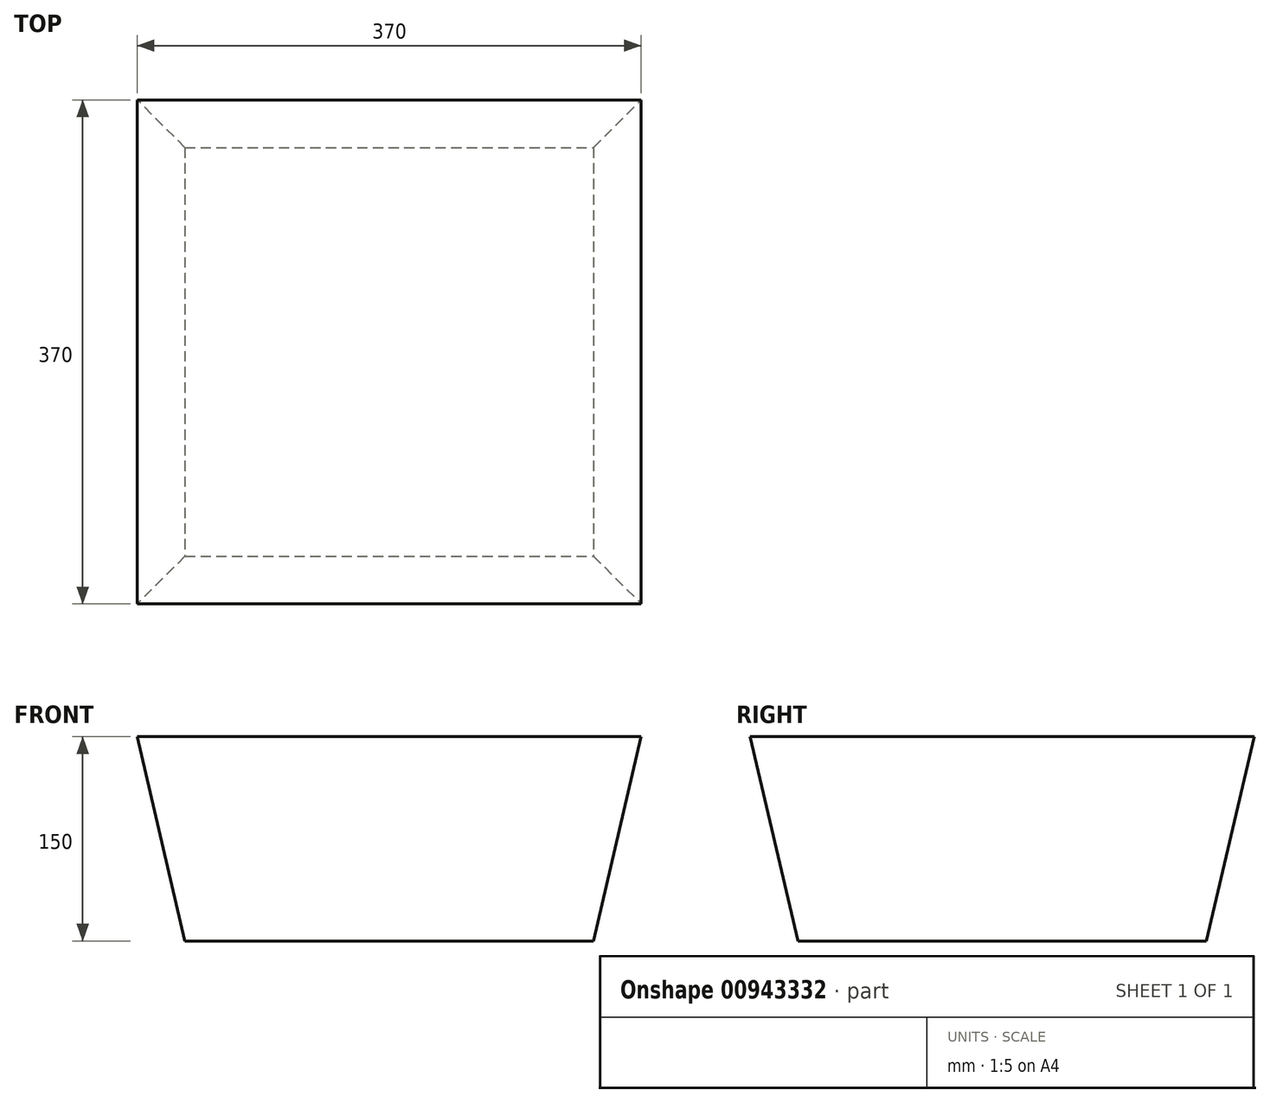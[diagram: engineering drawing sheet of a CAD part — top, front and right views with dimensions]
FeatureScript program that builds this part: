
annotation { "Feature Type Name" : "Feature", "Feature Type Description" : "" }
export const myFeature = defineFeature(function(context is Context, id is Id, definition is map)
    precondition{}
    {
        {
            var Q0;
            Q0=qCreatedBy(makeId("Top.planeOp"),FACE);
            var sketch = newSketch(context, id + "F0", { "sketchPlane" : qUnion([Q0])});
            skLineSegment(sketch, "E0.bottom", {"start": v(0, 0) * mm, "end": v(370, 0) * mm});
            skLineSegment(sketch, "E0.top", {"start": v(0, 370) * mm, "end": v(370, 370) * mm});
            skLineSegment(sketch, "E0.left", {"start": v(0, 0) * mm, "end": v(0, 370) * mm});
            skLineSegment(sketch, "E0.right", {"start": v(370, 0) * mm, "end": v(370, 370) * mm});
            skSolve(sketch);
        }
        {
            var Q0;
            Q0=qCreatedBy(makeId("Top.planeOp"),FACE);
            cPlane(context, id + "F1", {"entities" : qUnion([Q0]), "cplaneType" : CPlaneType.OFFSET, "offset" : 150 * mm, "oppositeDirection" : true, "width" : 150 * mm, "height" : 150 * mm});
        }
        {
            var Q0;
            Q0=qCreatedBy(id+"F1.planeOp",FACE);
            var sketch = newSketch(context, id + "F2", { "sketchPlane" : qUnion([Q0])});
            skLineSegment(sketch, "E1.bottom", {"start": v(35, 335) * mm, "end": v(335, 335) * mm});
            skLineSegment(sketch, "E1.top", {"start": v(35, 35) * mm, "end": v(335, 35) * mm});
            skLineSegment(sketch, "E1.left", {"start": v(35, 335) * mm, "end": v(35, 35) * mm});
            skLineSegment(sketch, "E1.right", {"start": v(335, 335) * mm, "end": v(335, 35) * mm});
            skSolve(sketch);
        }
        {
            var Q0;
            Q0=makeQuery(id+"F2.imprint","IMPRINT",FACE,{"disambiguationData":[TD([[makeQuery(id+"F2.imprint","IMPRINT",EDGE,{"derivedFrom":sQuery(id+"F2.wireOp",EDGE,"E1.bottom")}),-1.0]])]});
            var Q1;
            Q1=makeQuery(id+"F0.imprint","IMPRINT",FACE,{"disambiguationData":[TD([[makeQuery(id+"F0.imprint","IMPRINT",EDGE,{"derivedFrom":sQuery(id+"F0.wireOp",EDGE,"E0.bottom")}),1.0]])]});
            loft(context, id + "F3", {"sheetProfilesArray" : [{ "sheetProfileEntities" : qUnion([Q0]) }, { "sheetProfileEntities" : qUnion([Q1]) }]});
        }
    });
